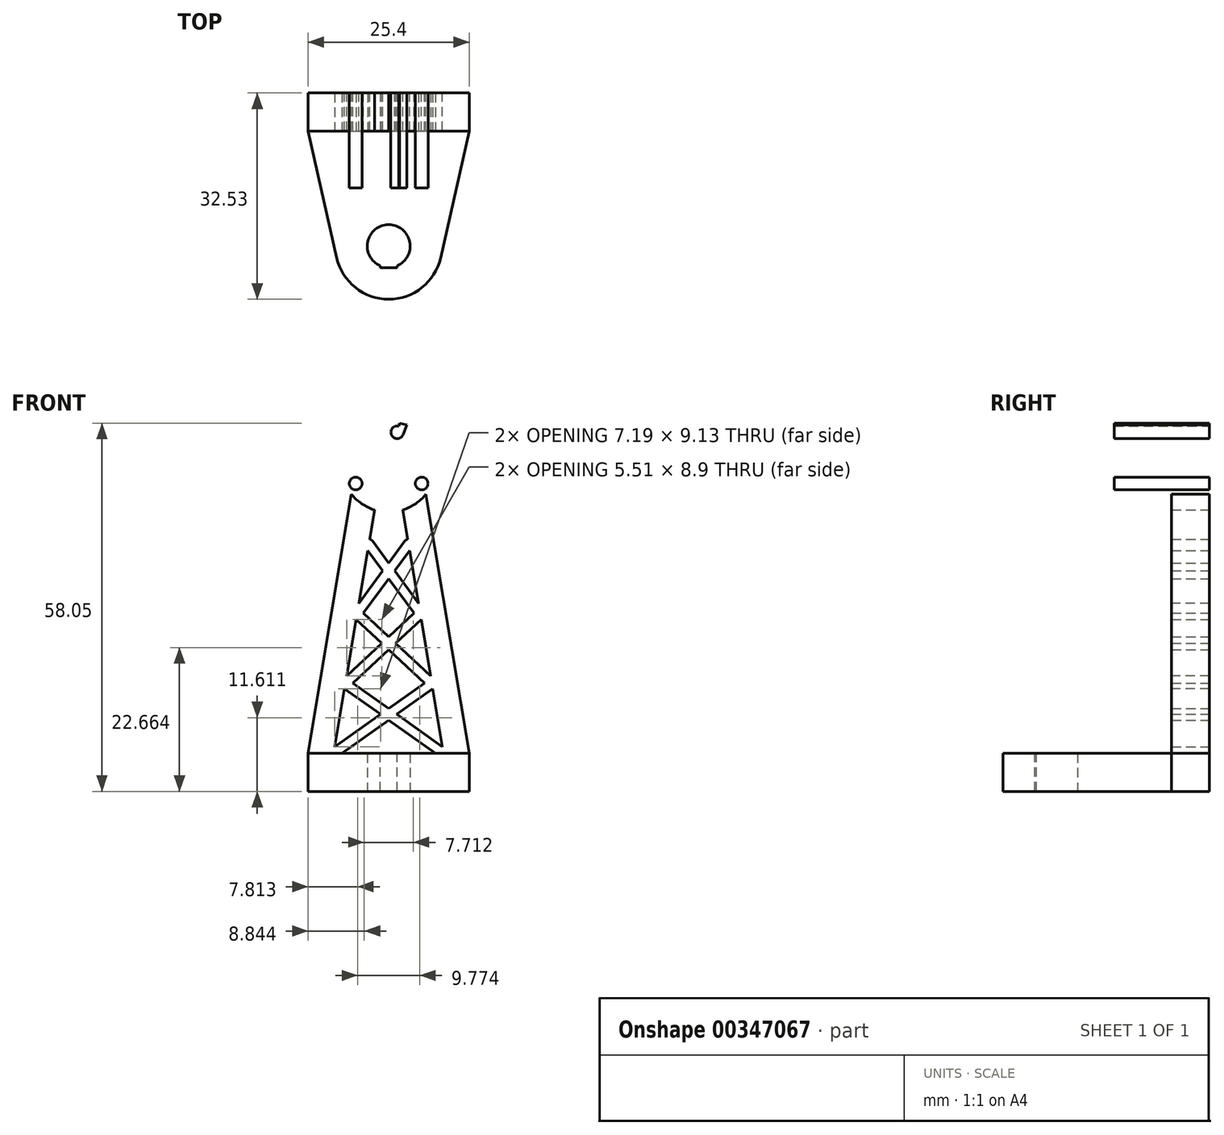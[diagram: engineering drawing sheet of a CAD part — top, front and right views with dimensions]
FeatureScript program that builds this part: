
annotation { "Feature Type Name" : "Feature", "Feature Type Description" : "" }
export const myFeature = defineFeature(function(context is Context, id is Id, definition is map)
    precondition{}
    {
        {
            var Q0;
            Q0=qCreatedBy(makeId("Right.planeOp"),FACE);
            var sketch = newSketch(context, id + "F0", { "sketchPlane" : qUnion([Q0])});
            skLineSegment(sketch, "E0", {"start": v(0, 51.52) * mm, "end": v(-22.53, 51.52) * mm, "construction": true});
            skSolve(sketch);
        }
        {
            var Q0;
            Q0=qCreatedBy(makeId("Front.planeOp"),FACE);
            var sketch = newSketch(context, id + "F1", { "sketchPlane" : qUnion([Q0])});
            skLineSegment(sketch, "E1.bottom", {"start": v(12.7, 0) * mm, "end": v(-12.7, 0) * mm});
            skLineSegment(sketch, "E1.top", {"start": v(12.7, 6) * mm, "end": v(-12.7, 6) * mm});
            skLineSegment(sketch, "E1.left", {"start": v(12.7, 0) * mm, "end": v(12.7, 6) * mm});
            skLineSegment(sketch, "E1.right", {"start": v(-12.7, 0) * mm, "end": v(-12.7, 6) * mm});
            skPoint(sketch, "E2.0", {"position": v(0, 51.52) * mm});
            skLineSegment(sketch, "E3.0", {"start": v(0, 57.53) * mm, "end": v(5.2, 48.52) * mm, "construction": true});
            skLineSegment(sketch, "E3.1", {"start": v(5.2, 48.52) * mm, "end": v(-5.2, 48.52) * mm, "construction": true});
            skLineSegment(sketch, "E3.2", {"start": v(-5.2, 48.53) * mm, "end": v(0, 57.53) * mm, "construction": true});
            skCircle(sketch, "E4", {"center": v(-5.2, 48.53) * mm, "radius": 1 * mm});
            skCircle(sketch, "E5", {"center": v(5.2, 48.53) * mm, "radius": 1 * mm});
            skArc(sketch, "E6", {"start": v(0, 57.53) * mm, "mid": v(0.7, 57.09) * mm, "end": v(1.35, 56.6) * mm, "construction": true});
            skCircle(sketch, "E7", {"center": v(1.35, 56.6) * mm, "radius": 1 * mm});
            skLineSegment(sketch, "E8", {"start": v(0, 51.52) * mm, "end": v(1.35, 56.6) * mm, "construction": true});
            skPoint(sketch, "E9", {"position": v(1.09, 55.63) * mm});
            skCircle(sketch, "E10", {"center": v(0, 51.52) * mm, "radius": 5 * mm, "construction": true});
            skArc(sketch, "E11", {"start": v(-4.63, 47.7) * mm, "mid": v(0, 45.53) * mm, "end": v(4.63, 47.7) * mm});
            skArc(sketch, "E12", {"start": v(4.63, 47.7) * mm, "mid": v(0, 57.52) * mm, "end": v(-4.63, 47.7) * mm, "construction": true});
            skArc(sketch, "E13.0", {"start": v(-7.03, 48.9) * mm, "mid": v(-0.48, 44.04) * mm, "end": v(6.64, 48.04) * mm});
            skLineSegment(sketch, "E14", {"start": v(0, 51.53) * mm, "end": v(-7.59, 48.7) * mm, "construction": true});
            skLineSegment(sketch, "E15", {"start": v(0, 51.52) * mm, "end": v(1.73, 58.05) * mm});
            skLineSegment(sketch, "E16", {"start": v(0, 51.53) * mm, "end": v(-7.24, 52.54) * mm, "construction": true});
            skLineSegment(sketch, "E17", {"start": v(0, 51.53) * mm, "end": v(-5.23, 56.36) * mm, "construction": true});
            skLineSegment(sketch, "E18", {"start": v(0, 51.53) * mm, "end": v(-1.78, 58.23) * mm, "construction": true});
            skFitSpline(sketch, "E19", {"points": [v(-7.03, 48.9) * mm, v(-7.24, 52.54) * mm, v(-5.23, 56.36) * mm, v(-1.78, 58.23) * mm, v(1.73, 58.05) * mm], "startDerivative": vector(-4.04, 15.96) * mm, "endDerivative": vector(19.6, -4.9) * mm});
            skFitSpline(sketch, "E20.0", {"points": [v(-5.58, 49.28) * mm, v(-5.65, 49.58) * mm, v(-5.78, 50.15) * mm, v(-5.87, 50.9) * mm, v(-5.87, 51.61) * mm, v(-5.77, 52.32) * mm, v(-5.55, 53.1) * mm, v(-5.22, 53.88) * mm, v(-4.85, 54.49) * mm, v(-4.52, 54.93) * mm, v(-4.25, 55.23) * mm, v(-3.97, 55.5) * mm, v(-3.55, 55.83) * mm, v(-2.98, 56.2) * mm, v(-2.37, 56.47) * mm, v(-1.89, 56.65) * mm, v(-1.54, 56.75) * mm, v(-1.22, 56.82) * mm, v(-0.93, 56.87) * mm, v(-0.65, 56.9) * mm, v(-0.25, 56.9) * mm, v(0.33, 56.83) * mm, v(0.99, 56.69) * mm, v(1.37, 56.6) * mm]});
            skLineSegment(sketch, "E21", {"start": v(1.73, 58.05) * mm, "end": v(2.86, 57.75) * mm});
            skLineSegment(sketch, "E22", {"start": v(2.86, 57.75) * mm, "end": v(2.28, 56.24) * mm});
            skLineSegment(sketch, "E23", {"start": v(6.64, 48.04) * mm, "end": v(7.08, 48.88) * mm});
            skLineSegment(sketch, "E24", {"start": v(7.08, 48.88) * mm, "end": v(5.55, 49.46) * mm});
            skLineSegment(sketch, "E25", {"start": v(0, 0) * mm, "end": v(0, -2.3) * mm, "construction": true});
            skLineSegment(sketch, "E26", {"start": v(-12.7, 6) * mm, "end": v(-5.87, 46.86) * mm});
            skLineSegment(sketch, "E27", {"start": v(-8.65, 6) * mm, "end": v(-2.24, 44.37) * mm});
            skLineSegment(sketch, "E28.MirrorCS", {"start": v(8.65, 6) * mm, "end": v(2.24, 44.37) * mm});
            skLineSegment(sketch, "E29.MirrorCS", {"start": v(12.7, 6) * mm, "end": v(5.87, 46.86) * mm});
            skSolve(sketch);
        }
        {
            var Q0;
            {var subQ2=sQuery(id+"F1.wireOp",EDGE,"E28.MirrorCS");Q0=makeQuery(id+"F1.imprint","IMPRINT",FACE,{"disambiguationData":[TD([[makeQuery(id+"F1.imprint","IMPRINT",EDGE,{"derivedFrom":subQ2}),-1.0]])]});}
            var Q1;
            {var subQ0=sQuery(id+"F1.wireOp",EDGE,"E26");Q1=makeQuery(id+"F1.imprint","IMPRINT",FACE,{"disambiguationData":[TD([[makeQuery(id+"F1.imprint","IMPRINT",EDGE,{"derivedFrom":subQ0}),-1.0]])]});}
            var Q2;
            {var subQ2=sQuery(id+"F1.wireOp",EDGE,"E28.MirrorCS");Q2=makeQuery(id+"F1.imprint","IMPRINT",FACE,{"disambiguationData":[TD([[makeQuery(id+"F1.imprint","IMPRINT",EDGE,{"derivedFrom":subQ2}),-1.0]])]});}
            var Q3;
            {var subQ0=sQuery(id+"F1.wireOp",EDGE,"E26");Q3=makeQuery(id+"F1.imprint","IMPRINT",FACE,{"disambiguationData":[TD([[makeQuery(id+"F1.imprint","IMPRINT",EDGE,{"derivedFrom":subQ0}),-1.0]])]});}
            var Q4;
            {var subQ2=sQuery(id+"F1.wireOp",EDGE,"E28.MirrorCS");Q4=makeQuery(id+"F1.imprint","IMPRINT",FACE,{"disambiguationData":[TD([[makeQuery(id+"F1.imprint","IMPRINT",EDGE,{"derivedFrom":subQ2}),-1.0]])]});}
            var Q5;
            {var subQ0=sQuery(id+"F1.wireOp",EDGE,"E26");Q5=makeQuery(id+"F1.imprint","IMPRINT",FACE,{"disambiguationData":[TD([[makeQuery(id+"F1.imprint","IMPRINT",EDGE,{"derivedFrom":subQ0}),-1.0]])]});}
            extrude(context, id + "F2", {"entities" : qUnion([Q0, Q1, Q2, Q3, Q4, Q5]), "depth" : 6 * mm});
        }
        {
            var Q0;
            {var subQ5=sQuery(id+"F1.wireOp",EDGE,"E11");Q0=makeQuery(id+"F1.imprint","IMPRINT",FACE,{"disambiguationData":[TD([[makeQuery(id+"F1.imprint","IMPRINT",EDGE,{"derivedFrom":subQ5}),-1.0]])]});}
            var Q1;
            {var subQ0=sQuery(id+"F1.wireOp",EDGE,"E4");var subQ1=makeQuery(id+"F1.imprint","INTERSECT",VERTEX,{"derivedFrom":[subQ0,sQuery(id+"F1.wireOp",EDGE,"E11")]});Q1=makeQuery(id+"F1.imprint","IMPRINT",FACE,{"disambiguationData":[TD([[makeQuery(id+"F1.imprint","IMPRINT",EDGE,{"disambiguationData":[TD([[subQ1,1.0]])],"derivedFrom":subQ0}),1.0]])]});}
            var Q2;
            {var subQ0=sQuery(id+"F1.wireOp",EDGE,"E5");var subQ1=makeQuery(id+"F1.imprint","INTERSECT",VERTEX,{"derivedFrom":[subQ0,sQuery(id+"F1.wireOp",EDGE,"E11")]});Q2=makeQuery(id+"F1.imprint","IMPRINT",FACE,{"disambiguationData":[TD([[makeQuery(id+"F1.imprint","IMPRINT",EDGE,{"disambiguationData":[TD([[subQ1,1.0]])],"derivedFrom":subQ0}),1.0]])]});}
            var Q3;
            {var subQ0=sQuery(id+"F1.wireOp",EDGE,"E7");var subQ1=makeQuery(id+"F1.imprint","INTERSECT",VERTEX,{"derivedFrom":[subQ0,sQuery(id+"F1.wireOp",EDGE,"E22")]});Q3=makeQuery(id+"F1.imprint","IMPRINT",FACE,{"disambiguationData":[TD([[makeQuery(id+"F1.imprint","IMPRINT",EDGE,{"disambiguationData":[TD([[subQ1,1.0]])],"derivedFrom":subQ0}),1.0]])]});}
            var Q4;
            {var subQ4=sQuery(id+"F1.wireOp",EDGE,"E21");Q4=makeQuery(id+"F1.imprint","IMPRINT",FACE,{"disambiguationData":[TD([[makeQuery(id+"F1.imprint","IMPRINT",EDGE,{"derivedFrom":subQ4}),-1.0]])]});}
            var Q5;
            {var subQ0=sQuery(id+"F1.wireOp",EDGE,"E20.0");var subQ1=sQuery(id+"F1.wireOp",EDGE,"E7");var subQ2=makeQuery(id+"F1.imprint","INTERSECT",VERTEX,{"derivedFrom":[subQ1,subQ0]});Q5=makeQuery(id+"F1.imprint","IMPRINT",FACE,{"disambiguationData":[TD([[makeQuery(id+"F1.imprint","IMPRINT",EDGE,{"disambiguationData":[TD([[subQ2,1.0]])],"derivedFrom":subQ1}),1.0]])]});}
            var Q6;
            {var subQ0=sQuery(id+"F1.wireOp",EDGE,"E15");var subQ1=sQuery(id+"F1.wireOp",EDGE,"E7");var subQ2=makeQuery(id+"F1.imprint","INTERSECT",VERTEX,{"disambiguationData":[OD(0.0)],"derivedFrom":[subQ1,subQ0]});Q6=makeQuery(id+"F1.imprint","IMPRINT",FACE,{"disambiguationData":[TD([[makeQuery(id+"F1.imprint","IMPRINT",EDGE,{"disambiguationData":[TD([[subQ2,1.0]])],"derivedFrom":subQ1}),1.0]])]});}
            extrude(context, id + "F3", {"entities" : qUnion([Q0, Q1, Q2, Q3, Q4, Q5, Q6]), "operationType" : NewBodyOperationType.ADD, "depth" : 15 * mm});
        }
        {
            var Q0;
            Q0=makeQuery(id+"F1.imprint","IMPRINT",FACE,{"disambiguationData":[TD([[makeQuery(id+"F1.imprint","IMPRINT",EDGE,{"derivedFrom":sQuery(id+"F1.wireOp",EDGE,"E1.bottom")}),-1.0]])]});
            extrude(context, id + "F4", {"entities" : qUnion([Q0]), "operationType" : NewBodyOperationType.ADD, "depth" : 35 * mm});
        }
        {
            var Q0;
            {var subQ2=sQuery(id+"F1.wireOp",EDGE,"E28.MirrorCS");Q0=makeQuery(id+"F1.imprint","IMPRINT",FACE,{"disambiguationData":[TD([[makeQuery(id+"F1.imprint","IMPRINT",EDGE,{"derivedFrom":subQ2}),-1.0]])]});}
            var sketch = newSketch(context, id + "F5", { "sketchPlane" : qUnion([Q0])});
            skLineSegment(sketch, "E30.0", {"start": v(12.7, 6) * mm, "end": v(-12.7, 6) * mm, "construction": true});
            skPoint(sketch, "E31.0", {"position": v(0, -1.15) * mm});
            skLineSegment(sketch, "E32.0", {"start": v(0, 0) * mm, "end": v(0, -2.3) * mm, "construction": true});
            skLineSegment(sketch, "E33.0.1.0", {"start": v(12.7, 17) * mm, "end": v(-12.7, 17) * mm, "construction": true});
            skLineSegment(sketch, "E33.0.2.0", {"start": v(12.7, 28) * mm, "end": v(-12.7, 28) * mm, "construction": true});
            skLineSegment(sketch, "E33.0.3.0", {"start": v(12.7, 39) * mm, "end": v(-12.7, 39) * mm, "construction": true});
            skLineSegment(sketch, "E33.0.4.0", {"start": v(12.7, 50) * mm, "end": v(-12.7, 50) * mm, "construction": true});
            skLineSegment(sketch, "E33.direction1", {"start": v(-12.7, 6) * mm, "end": v(12.3, 6) * mm, "construction": true});
            skLineSegment(sketch, "E33.direction2", {"start": v(-12.7, 6) * mm, "end": v(-12.7, 17) * mm, "construction": true});
            skLineSegment(sketch, "E34.0", {"start": v(-8.65, 6) * mm, "end": v(-2.24, 44.37) * mm, "construction": true});
            skLineSegment(sketch, "E35.0", {"start": v(8.65, 6) * mm, "end": v(2.24, 44.37) * mm, "construction": true});
            skArc(sketch, "E36.0.startCap", {"start": v(6.38, 17.61) * mm, "mid": v(7.43, 17.43) * mm, "end": v(7.25, 16.39) * mm});
            skArc(sketch, "E36.0.endCap", {"start": v(-8.22, 5.39) * mm, "mid": v(-9.27, 5.57) * mm, "end": v(-9.09, 6.61) * mm});
            skLineSegment(sketch, "E36.0.left", {"start": v(7.25, 16.39) * mm, "end": v(-8.22, 5.39) * mm});
            skLineSegment(sketch, "E36.0.right", {"start": v(6.38, 17.61) * mm, "end": v(-9.09, 6.61) * mm});
            skLineSegment(sketch, "E37.MirrorCS", {"start": v(-7.25, 16.39) * mm, "end": v(8.22, 5.39) * mm});
            skLineSegment(sketch, "E38.MirrorCS", {"start": v(-6.38, 17.61) * mm, "end": v(9.09, 6.61) * mm});
            skArc(sketch, "E39.MirrorCS", {"start": v(-6.38, 17.61) * mm, "mid": v(-7.43, 17.43) * mm, "end": v(-7.25, 16.39) * mm});
            skArc(sketch, "E40.MirrorCS", {"start": v(8.22, 5.39) * mm, "mid": v(9.27, 5.57) * mm, "end": v(9.09, 6.61) * mm});
            skArc(sketch, "E41.0.startCap", {"start": v(-4.37, 27.55) * mm, "mid": v(-5.42, 27.4) * mm, "end": v(-5.58, 28.45) * mm});
            skArc(sketch, "E41.0.endCap", {"start": v(2.53, 39.45) * mm, "mid": v(3.58, 39.6) * mm, "end": v(3.74, 38.55) * mm});
            skLineSegment(sketch, "E41.0.left", {"start": v(-5.58, 28.45) * mm, "end": v(2.53, 39.45) * mm});
            skLineSegment(sketch, "E41.0.right", {"start": v(-4.37, 27.55) * mm, "end": v(3.74, 38.55) * mm});
            skArc(sketch, "E41.1.startCap", {"start": v(-6.3, 16.45) * mm, "mid": v(-7.36, 16.49) * mm, "end": v(-7.33, 17.55) * mm});
            skArc(sketch, "E41.1.endCap", {"start": v(4.47, 28.55) * mm, "mid": v(5.53, 28.51) * mm, "end": v(5.49, 27.45) * mm});
            skLineSegment(sketch, "E41.1.left", {"start": v(-7.33, 17.55) * mm, "end": v(4.47, 28.55) * mm});
            skLineSegment(sketch, "E41.1.right", {"start": v(-6.3, 16.45) * mm, "end": v(5.49, 27.45) * mm});
            skLineSegment(sketch, "E42.MirrorCS", {"start": v(7.33, 17.55) * mm, "end": v(-4.47, 28.55) * mm});
            skLineSegment(sketch, "E43.MirrorCS", {"start": v(6.3, 16.45) * mm, "end": v(-5.49, 27.45) * mm});
            skLineSegment(sketch, "E44.MirrorCS", {"start": v(5.58, 28.45) * mm, "end": v(-2.53, 39.45) * mm});
            skLineSegment(sketch, "E45.MirrorCS", {"start": v(4.37, 27.55) * mm, "end": v(-3.74, 38.55) * mm});
            skArc(sketch, "E46.MirrorCS", {"start": v(6.3, 16.45) * mm, "mid": v(7.36, 16.49) * mm, "end": v(7.33, 17.55) * mm});
            skArc(sketch, "E47.MirrorCS", {"start": v(4.37, 27.55) * mm, "mid": v(5.42, 27.4) * mm, "end": v(5.58, 28.45) * mm});
            skArc(sketch, "E48.MirrorCS", {"start": v(-2.53, 39.45) * mm, "mid": v(-3.58, 39.6) * mm, "end": v(-3.74, 38.55) * mm});
            skSolve(sketch);
        }
        {
            var Q0;
            Q0 = qSketchRegion(id + "F5", true);
            extrude(context, id + "F6", {"entities" : qUnion([Q0]), "operationType" : NewBodyOperationType.ADD, "depth" : 6 * mm});
        }
        {
            var Q0;
            Q0=makeQuery(id+"F4.opExtrude","SWEPT_FACE",FACE,{"disambiguationData":[OSD([sQuery(id+"F1.wireOp",EDGE,"E1.top")])]});
            var sketch = newSketch(context, id + "F7", { "sketchPlane" : qUnion([Q0])});
            skLineSegment(sketch, "E49.0", {"start": v(0, 0) * mm, "end": v(0, -40) * mm, "construction": true});
            skPoint(sketch, "E50", {"position": v(0, -24.15) * mm});
            skSolve(sketch);
        }
        {
            var Q0;
            Q0=sQuery(id+"F7.wireOp",VERTEX,"E50");
            var Q1;
            Q1=makeQuery(id+"F2.opExtrude","SWEPT_BODY",BODY,{"disambiguationData":[OSD([sQuery(id+"F1.wireOp",EDGE,"E1.top"),sQuery(id+"F1.wireOp",EDGE,"E13.0"),sQuery(id+"F1.wireOp",EDGE,"E28.MirrorCS"),sQuery(id+"F1.wireOp",EDGE,"E29.MirrorCS")])]});
            hole(context, id + "F8", {"style" : HoleStyle.SIMPLE, "endStyle" : HoleEndStyle.THROUGH, "standardTappedOrClearance" : lookupTablePath({ "standard" : "ANSI", "fit" : "Normal (ASME)", "size" : "1/4", "type" : "Clearance" }), "standardBlindInLast" : lookupTablePath({ "fit" : "Free", "standard" : "ANSI", "size" : "1/4", "type" : "Clearance" }), "holeDiameter" : 6.76 * mm, "isTappedThrough" : true, "tappedDepth" : 12 * mm, "tapClearance" : 3, "locations" : qUnion([Q0]), "scope" : qUnion([Q1]), "startStyle" : HoleStartStyle.PART});
        }
        {
            var Q0;
            Q0=makeQuery(id+"F4.opExtrude","SWEPT_FACE",FACE,{"disambiguationData":[OSD([sQuery(id+"F1.wireOp",EDGE,"E1.top")])]});
            var sketch = newSketch(context, id + "F9", { "sketchPlane" : qUnion([Q0])});
            skCircle(sketch, "E51.0", {"center": v(0, -24.15) * mm, "radius": 3.38 * mm});
            skCircle(sketch, "E52.0", {"center": v(0, -24.15) * mm, "radius": 8.38 * mm});
            skLineSegment(sketch, "E53", {"start": v(-12.7, -6) * mm, "end": v(-8.17, -26) * mm});
            skLineSegment(sketch, "E54.MirrorCS", {"start": v(12.7, -6) * mm, "end": v(8.17, -26) * mm});
            skLineSegment(sketch, "E55.0.0", {"start": v(7.36, -6) * mm, "end": v(7.36, 0) * mm});
            skLineSegment(sketch, "E55.0.1", {"start": v(7.36, 0) * mm, "end": v(-7.36, 0) * mm});
            skLineSegment(sketch, "E55.0.2", {"start": v(-7.36, 0) * mm, "end": v(-7.36, -6) * mm});
            skLineSegment(sketch, "E55.0.3", {"start": v(-7.36, -6) * mm, "end": v(-12.7, -6) * mm});
            skLineSegment(sketch, "E55.0.4", {"start": v(-12.7, -6) * mm, "end": v(-12.7, -35) * mm});
            skLineSegment(sketch, "E55.0.5", {"start": v(-12.7, -35) * mm, "end": v(12.7, -35) * mm});
            skLineSegment(sketch, "E55.0.6", {"start": v(12.7, -35) * mm, "end": v(12.7, -6) * mm});
            skLineSegment(sketch, "E55.0.7", {"start": v(12.7, -6) * mm, "end": v(7.36, -6) * mm});
            skLineSegment(sketch, "E56.bottom", {"start": v(0, -27.53) * mm, "end": v(-1.34, -27.53) * mm});
            skLineSegment(sketch, "E56.top", {"start": v(0, -27.25) * mm, "end": v(-1.34, -27.25) * mm});
            skLineSegment(sketch, "E56.left", {"start": v(0, -27.53) * mm, "end": v(0, -27.25) * mm});
            skLineSegment(sketch, "E56.right", {"start": v(-1.34, -27.53) * mm, "end": v(-1.34, -27.25) * mm});
            skLineSegment(sketch, "E57.MirrorCS", {"start": v(1.34, -27.53) * mm, "end": v(1.34, -27.25) * mm});
            skLineSegment(sketch, "E58.MirrorCS", {"start": v(0, -27.53) * mm, "end": v(1.34, -27.53) * mm});
            skLineSegment(sketch, "E59.MirrorCS", {"start": v(0, -27.25) * mm, "end": v(1.34, -27.25) * mm});
            skSolve(sketch);
        }
        {
            var Q0;
            {var subQ2=sQuery(id+"F9.wireOp",EDGE,"E53");Q0=makeQuery(id+"F9.imprint","IMPRINT",FACE,{"disambiguationData":[TD([[makeQuery(id+"F9.imprint","IMPRINT",EDGE,{"derivedFrom":subQ2}),-1.0]])]});}
            var Q1;
            {var subQ0=sQuery(id+"F9.wireOp",EDGE,"xUyw8eTe-UIbE-ToAb-zEbA-Q9IoFuOnh57A.bottom");Q1=makeQuery(id+"F9.imprint","IMPRINT",FACE,{"disambiguationData":[TD([[makeQuery(id+"F9.imprint","IMPRINT",EDGE,{"derivedFrom":subQ0}),1.0]])]});}
            var Q2;
            {var subQ2=sQuery(id+"F9.wireOp",EDGE,"xUyw8eTe-UIbE-ToAb-zEbA-Q9IoFuOnh57A.top");Q2=makeQuery(id+"F9.imprint","IMPRINT",FACE,{"disambiguationData":[TD([[makeQuery(id+"F9.imprint","IMPRINT",EDGE,{"derivedFrom":subQ2}),-1.0]])]});}
            var Q3;
            {var subQ0=sQuery(id+"F9.wireOp",EDGE,"07fd9ac6-7763-4ba3-87b8-021d76b749820.MirrorCS");Q3=makeQuery(id+"F9.imprint","IMPRINT",FACE,{"disambiguationData":[TD([[makeQuery(id+"F9.imprint","IMPRINT",EDGE,{"derivedFrom":subQ0}),1.0]])]});}
            var Q4;
            {var subQ0=sQuery(id+"F9.wireOp",EDGE,"42ddb8a6-7881-494d-ae35-8b5b128752ca0.MirrorCS");Q4=makeQuery(id+"F9.imprint","IMPRINT",FACE,{"disambiguationData":[TD([[makeQuery(id+"F9.imprint","IMPRINT",EDGE,{"derivedFrom":subQ0}),-1.0]])]});}
            var Q5;
            {var subQ0=sQuery(id+"F9.wireOp",EDGE,"1l93E8Bl-ekRN-WoCz-yVk5-KYtULoFQYGXU");Q5=makeQuery(id+"F9.imprint","IMPRINT",FACE,{"disambiguationData":[TD([[makeQuery(id+"F9.imprint","IMPRINT",EDGE,{"derivedFrom":subQ0}),-1.0]])]});}
            var Q6;
            {var subQ0=sQuery(id+"F9.wireOp",EDGE,"E57.MirrorCS");Q6=makeQuery(id+"F9.imprint","IMPRINT",FACE,{"disambiguationData":[TD([[makeQuery(id+"F9.imprint","IMPRINT",EDGE,{"derivedFrom":subQ0}),1.0]])]});}
            var Q7;
            {var subQ0=sQuery(id+"F9.wireOp",EDGE,"E56.bottom");Q7=makeQuery(id+"F9.imprint","IMPRINT",FACE,{"disambiguationData":[TD([[makeQuery(id+"F9.imprint","IMPRINT",EDGE,{"derivedFrom":subQ0}),-1.0]])]});}
            var Q8;
            Q8=makeQuery(id+"F2.opExtrude","SWEPT_BODY",BODY,{"disambiguationData":[OSD([sQuery(id+"F1.wireOp",EDGE,"E1.top"),sQuery(id+"F1.wireOp",EDGE,"E13.0"),sQuery(id+"F1.wireOp",EDGE,"E28.MirrorCS"),sQuery(id+"F1.wireOp",EDGE,"E29.MirrorCS")])]});
            extrude(context, id + "F10", {"entities" : qUnion([Q0, Q1, Q2, Q3, Q4, Q5, Q6, Q7]), "operationType" : NewBodyOperationType.REMOVE, "endBound" : BoundingType.UP_TO_BODY, "oppositeDirection" : true, "endBoundEntityBody" : qUnion([Q8]), "depth" : 25 * mm, "offsetDistance" : 25 * mm});
        }
    });
